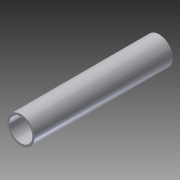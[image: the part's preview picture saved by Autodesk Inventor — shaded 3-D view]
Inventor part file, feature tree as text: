
AUTODESK INVENTOR PART (.ipt)
format: ipt  version: 2015 (Build 190159000, 159)  size: 79,360 bytes
history: native  units: in
note: dims shown in document units (in); Inventor stores cm internally (conversion verified against a paired STEP export)
features: extrude x1, sketch x1
ambient origin geometry x8: Origin, YZ Plane, XZ Plane, XY Plane, X Axis, Y Axis, Z Axis, Center Point
bodies: Solid1 (feature_tree)
feature tree (2):
  extrude  "Extrusion1"  Depth=12.0in
  sketch  "Sketch1"  dims[d0=2.0in d1=2.375in d2=12.0in d3=0.0in]
